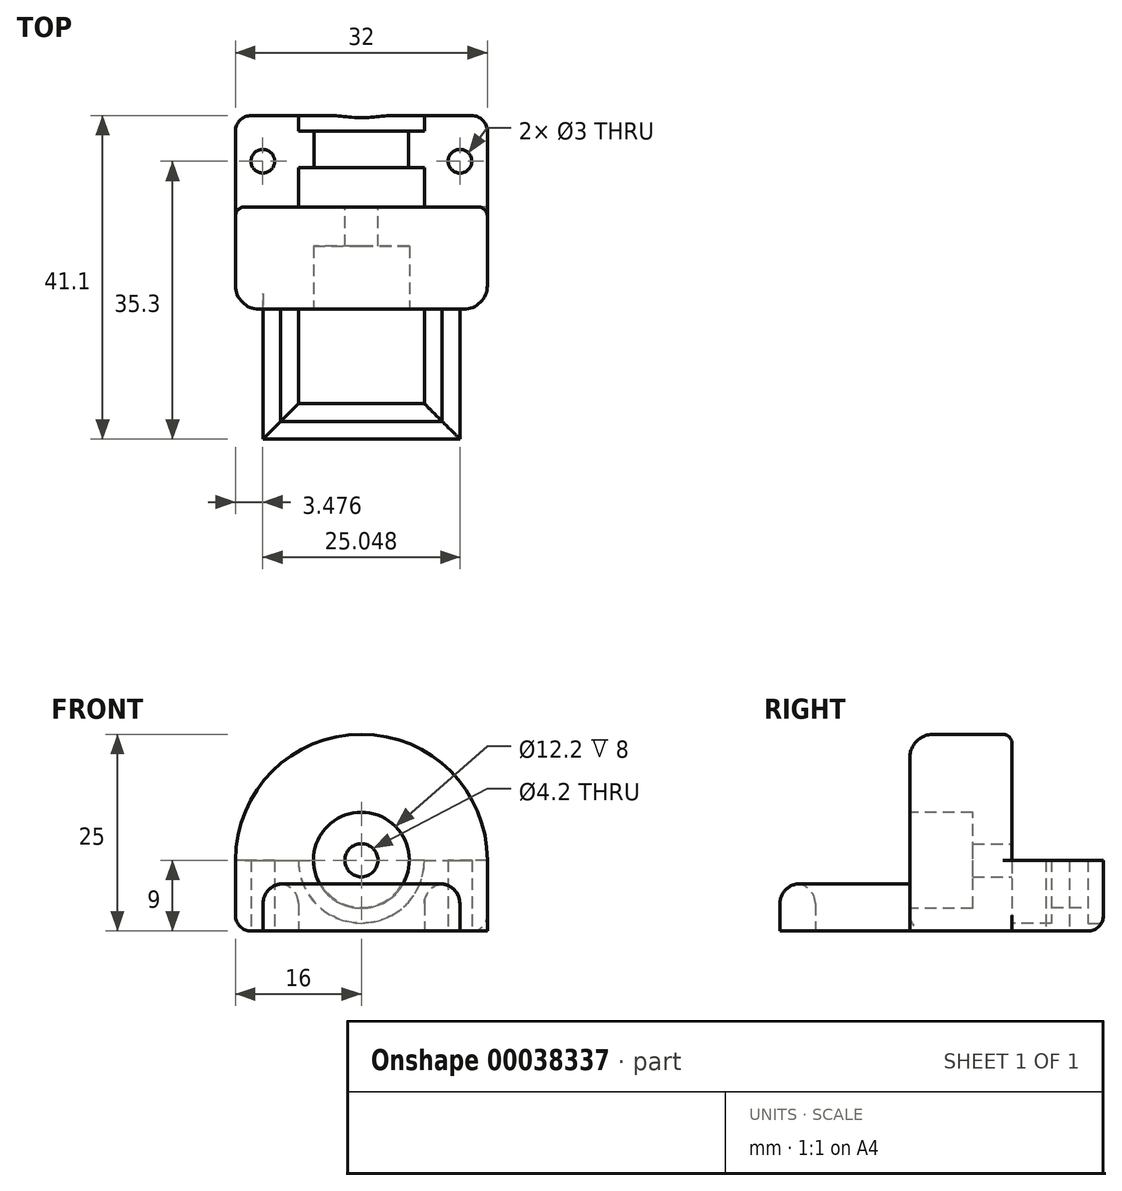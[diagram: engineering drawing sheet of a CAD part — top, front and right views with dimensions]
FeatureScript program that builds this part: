
annotation { "Feature Type Name" : "Feature", "Feature Type Description" : "" }
export const myFeature = defineFeature(function(context is Context, id is Id, definition is map)
    precondition{}
    {
        {
            var Q0;
            Q0=qCreatedBy(makeId("Top.planeOp"),FACE);
            var sketch = newSketch(context, id + "F0", { "sketchPlane" : qUnion([Q0])});
            skLineSegment(sketch, "E0.rect.bottom", {"start": v(-16, 5.8) * mm, "end": v(16, 5.8) * mm});
            skLineSegment(sketch, "E0.rect.top", {"start": v(-16, -5.8) * mm, "end": v(16, -5.8) * mm});
            skLineSegment(sketch, "E0.rect.left", {"start": v(-16, 5.8) * mm, "end": v(-16, -5.8) * mm});
            skLineSegment(sketch, "E0.rect.right", {"start": v(16, 5.8) * mm, "end": v(16, -5.8) * mm});
            skPoint(sketch, "E0.rect.middle", {"position": v(0, 0) * mm});
            skCircle(sketch, "E1", {"center": v(12.52, 0) * mm, "radius": 1.5 * mm});
            skCircle(sketch, "E2", {"center": v(-12.52, 0) * mm, "radius": 1.5 * mm});
            skSolve(sketch);
        }
        {
            var Q0;
            Q0=makeQuery(id+"F0.imprint","IMPRINT",FACE,{"disambiguationData":[TD([[makeQuery(id+"F0.imprint","IMPRINT",EDGE,{"derivedFrom":sQuery(id+"F0.wireOp",EDGE,"E0.rect.bottom")}),-1.0]])]});
            extrude(context, id + "F1", {"entities" : qUnion([Q0]), "depth" : 9 * mm});
        }
        {
            var Q0;
            Q0=makeQuery(id+"F1.opExtrude","SWEPT_FACE",FACE,{"disambiguationData":[OSD([sQuery(id+"F0.wireOp",EDGE,"E0.rect.top")])]});
            var sketch = newSketch(context, id + "F2", { "sketchPlane" : qUnion([Q0])});
            skCircle(sketch, "E3", {"center": v(0, 9) * mm, "radius": 8 * mm});
            skSolve(sketch);
        }
        {
            var Q0;
            Q0=qSketchRegion(id+"F2",true);
            var Q1;
            Q1=makeQuery(id+"F1.opExtrude","SWEPT_FACE",FACE,{"disambiguationData":[OSD([sQuery(id+"F0.wireOp",EDGE,"E0.rect.bottom")])]});
            extrude(context, id + "F3", {"entities" : qUnion([Q0, Q1]), "operationType" : NewBodyOperationType.REMOVE, "oppositeDirection" : true, "depth" : 5 * mm});
        }
        {
            var Q0;
            Q0=makeQuery(id+"F1.opExtrude","SWEPT_FACE",FACE,{"disambiguationData":[OSD([sQuery(id+"F0.wireOp",EDGE,"E0.rect.bottom")])]});
            var sketch = newSketch(context, id + "F4", { "sketchPlane" : qUnion([Q0])});
            skCircle(sketch, "E4", {"center": v(0, 9) * mm, "radius": 8 * mm});
            skSolve(sketch);
        }
        {
            var Q0;
            Q0=qSketchRegion(id+"F4",true);
            extrude(context, id + "F5", {"entities" : qUnion([Q0]), "operationType" : NewBodyOperationType.REMOVE, "oppositeDirection" : true, "depth" : 2 * mm});
        }
        {
            var Q0;
            Q0=makeQuery(id+"F5.boolean.opBoolean","COPY",FACE,{"derivedFrom":makeQuery(id+"F5.opExtrude","CAP_FACE",FACE,{"disambiguationData":[OSD([sQuery(id+"F4.wireOp",EDGE,"E4")])],"isStart":false})});
            var sketch = newSketch(context, id + "F6", { "sketchPlane" : qUnion([Q0])});
            skCircle(sketch, "E5", {"center": v(0, 9) * mm, "radius": 6 * mm});
            skSolve(sketch);
        }
        {
            var Q0;
            Q0=qSketchRegion(id+"F6",true);
            extrude(context, id + "F7", {"entities" : qUnion([Q0]), "operationType" : NewBodyOperationType.REMOVE, "oppositeDirection" : true, "depth" : 25 * mm});
        }
        {
            var Q0;
            Q0=makeQuery(id+"F1.opExtrude","CAP_EDGE",EDGE,{"disambiguationData":[OSD([sQuery(id+"F0.wireOp",EDGE,"E0.rect.bottom")])],"isStart":true});
            var Q1;
            Q1=makeQuery(id+"F7.boolean.opBoolean","COPY",EDGE,{"derivedFrom":makeQuery(id+"F7.opExtrude","CAP_EDGE",EDGE,{"disambiguationData":[OSD([sQuery(id+"F6.wireOp",EDGE,"E5")])],"isStart":true})});
            var Q2;
            Q2=makeQuery(id+"F1.opExtrude","SWEPT_EDGE",EDGE,{"disambiguationData":[OSD([sQuery(id+"F0.wireOp",EDGE,"E0.rect.bottom"),sQuery(id+"F0.wireOp",EDGE,"E0.rect.left")])]});
            var Q3;
            Q3=makeQuery(id+"F1.opExtrude","CAP_EDGE",EDGE,{"disambiguationData":[OSD([sQuery(id+"F0.wireOp",EDGE,"E0.rect.left")])],"isStart":true});
            var Q4;
            Q4=makeQuery(id+"F1.opExtrude","CAP_EDGE",EDGE,{"disambiguationData":[OSD([sQuery(id+"F0.wireOp",EDGE,"E0.rect.right")])],"isStart":true});
            var Q5;
            Q5=makeQuery(id+"F1.opExtrude","SWEPT_EDGE",EDGE,{"disambiguationData":[OSD([sQuery(id+"F0.wireOp",EDGE,"E0.rect.bottom"),sQuery(id+"F0.wireOp",EDGE,"E0.rect.right")])]});
            fillet(context, id + "F8", {"entities" : qUnion([Q0, Q1, Q2, Q3, Q4, Q5]), "radius" : 2 * mm, "tangentPropagation" : true, "allowEdgeOverflow" : false});
        }
        {
            var Q0;
            Q0=makeQuery(id+"F1.opExtrude","SWEPT_FACE",FACE,{"disambiguationData":[OSD([sQuery(id+"F0.wireOp",EDGE,"E0.rect.top")])]});
            var sketch = newSketch(context, id + "F9", { "sketchPlane" : qUnion([Q0])});
            skArc(sketch, "E6", {"start": v(16, 9) * mm, "mid": v(0, 25) * mm, "end": v(-16, 9) * mm});
            skLineSegment(sketch, "E7", {"start": v(0, 0) * mm, "end": v(13.23, 0) * mm});
            skLineSegment(sketch, "E8", {"start": v(-13.23, 0) * mm, "end": v(0, 0) * mm});
            skLineSegment(sketch, "E9", {"start": v(-16, 9) * mm, "end": v(-16, 0) * mm});
            skLineSegment(sketch, "E10", {"start": v(16, 9) * mm, "end": v(16, 0) * mm});
            skLineSegment(sketch, "E11", {"start": v(-16, 0) * mm, "end": v(16, 0) * mm});
            skSolve(sketch);
        }
        {
            var Q0;
            Q0=qSketchRegion(id+"F9",true);
            extrude(context, id + "F10", {"entities" : qUnion([Q0]), "operationType" : NewBodyOperationType.ADD, "depth" : 13 * mm});
        }
        {
            var Q0;
            Q0=qCreatedBy(makeId("Top.planeOp"),FACE);
            var sketch = newSketch(context, id + "F11", { "sketchPlane" : qUnion([Q0])});
            skLineSegment(sketch, "E12", {"start": v(-8, -18.8) * mm, "end": v(-12.5, -18.8) * mm});
            skLineSegment(sketch, "E13", {"start": v(-12.5, -18.8) * mm, "end": v(-8, -18.8) * mm});
            skLineSegment(sketch, "E14", {"start": v(12.5, -18.8) * mm, "end": v(12.5, -35.3) * mm});
            skLineSegment(sketch, "E15", {"start": v(12.5, -35.3) * mm, "end": v(-12.5, -35.3) * mm});
            skLineSegment(sketch, "E16", {"start": v(-12.5, -35.3) * mm, "end": v(-12.5, -18.8) * mm});
            skLineSegment(sketch, "E17", {"start": v(-8, -18.8) * mm, "end": v(-8, -30.8) * mm});
            skLineSegment(sketch, "E18", {"start": v(-8, -30.8) * mm, "end": v(8, -30.8) * mm});
            skLineSegment(sketch, "E19", {"start": v(8, -30.8) * mm, "end": v(8, -18.8) * mm});
            skLineSegment(sketch, "E20.trimOffspring", {"start": v(8, -18.8) * mm, "end": v(12.5, -18.8) * mm});
            skPoint(sketch, "E21.orphan", {"position": v(0, -18.8) * mm});
            skPoint(sketch, "E22", {"position": v(0, -30.8) * mm});
            skPoint(sketch, "E23", {"position": v(0, -35.3) * mm});
            skSolve(sketch);
        }
        {
            var Q0;
            Q0=qSketchRegion(id+"F11",true);
            extrude(context, id + "F12", {"entities" : qUnion([Q0]), "operationType" : NewBodyOperationType.ADD, "depth" : 6 * mm});
        }
        {
            var Q0;
            Q0=makeQuery(id+"F12.opExtrude","CAP_EDGE",EDGE,{"disambiguationData":[OSD([sQuery(id+"F11.wireOp",EDGE,"E17")])],"isStart":false});
            var Q1;
            Q1=makeQuery(id+"F12.opExtrude","CAP_EDGE",EDGE,{"disambiguationData":[OSD([sQuery(id+"F11.wireOp",EDGE,"E16")])],"isStart":false});
            var Q2;
            Q2=makeQuery(id+"F12.opExtrude","CAP_EDGE",EDGE,{"disambiguationData":[OSD([sQuery(id+"F11.wireOp",EDGE,"E19")])],"isStart":false});
            var Q3;
            Q3=makeQuery(id+"F12.opExtrude","CAP_EDGE",EDGE,{"disambiguationData":[OSD([sQuery(id+"F11.wireOp",EDGE,"E14")])],"isStart":false});
            var Q4;
            Q4=makeQuery(id+"F12.opExtrude","CAP_EDGE",EDGE,{"disambiguationData":[OSD([sQuery(id+"F11.wireOp",EDGE,"E18")])],"isStart":false});
            var Q5;
            Q5=makeQuery(id+"F12.opExtrude","CAP_EDGE",EDGE,{"disambiguationData":[OSD([sQuery(id+"F11.wireOp",EDGE,"E15")])],"isStart":false});
            fillet(context, id + "F13", {"entities" : qUnion([Q0, Q1, Q2, Q3, Q4, Q5]), "radius" : 2.5 * mm, "tangentPropagation" : true, "allowEdgeOverflow" : false});
        }
        {
            var Q0;
            Q0=makeQuery(id+"F10.opExtrude","CAP_EDGE",EDGE,{"disambiguationData":[OSD([sQuery(id+"F9.wireOp",EDGE,"E6")])],"isStart":false});
            fillet(context, id + "F14", {"entities" : qUnion([Q0]), "radius" : 3 * mm, "tangentPropagation" : true, "allowEdgeOverflow" : false});
        }
        {
            var Q0;
            Q0=makeQuery(id+"F10.opExtrude","CAP_EDGE",EDGE,{"disambiguationData":[OSD([sQuery(id+"F9.wireOp",EDGE,"E6")])],"isStart":true});
            fillet(context, id + "F15", {"entities" : qUnion([Q0]), "radius" : 1.2 * mm, "tangentPropagation" : true, "allowEdgeOverflow" : false});
        }
        {
            var Q0;
            Q0=makeQuery(id+"F10.opExtrude","CAP_FACE",FACE,{"disambiguationData":[OSD([sQuery(id+"F9.wireOp",EDGE,"E6"),sQuery(id+"F9.wireOp",EDGE,"E9"),sQuery(id+"F9.wireOp",EDGE,"E10"),sQuery(id+"F9.wireOp",EDGE,"E11")])],"isStart":false});
            var sketch = newSketch(context, id + "F16", { "sketchPlane" : qUnion([Q0])});
            skCircle(sketch, "E24", {"center": v(0, 9) * mm, "radius": 6.1 * mm});
            skSolve(sketch);
        }
        {
            var Q0;
            Q0=qSketchRegion(id+"F16",true);
            extrude(context, id + "F17", {"entities" : qUnion([Q0]), "operationType" : NewBodyOperationType.REMOVE, "oppositeDirection" : true, "depth" : 8 * mm});
        }
        {
            var Q0;
            Q0=makeQuery(id+"F14.opFillet","BLEND_EDGE",EDGE,{"blendedFrom":[makeQuery(id+"F10.opExtrude","CAP_EDGE",EDGE,{"disambiguationData":[OSD([sQuery(id+"F9.wireOp",EDGE,"E9")])],"isStart":false}),makeQuery(id+"F10.boolean.opBoolean","MERGE",FACE,{"derivedFrom":[makeQuery(id+"F1.opExtrude","CAP_FACE",FACE,{"disambiguationData":[OSD([sQuery(id+"F0.wireOp",EDGE,"E0.rect.bottom"),sQuery(id+"F0.wireOp",EDGE,"E0.rect.top"),sQuery(id+"F0.wireOp",EDGE,"E0.rect.left"),sQuery(id+"F0.wireOp",EDGE,"E0.rect.right"),sQuery(id+"F0.wireOp",EDGE,"E1"),sQuery(id+"F0.wireOp",EDGE,"E2")])],"isStart":true}),makeQuery(id+"F10.opExtrude","SWEPT_FACE",FACE,{"disambiguationData":[OSD([sQuery(id+"F9.wireOp",EDGE,"E11")])]})]})],"blendedInto":[makeQuery(id+"F10.boolean.opBoolean","MERGE",FACE,{"derivedFrom":[makeQuery(id+"F1.opExtrude","CAP_FACE",FACE,{"disambiguationData":[OSD([sQuery(id+"F0.wireOp",EDGE,"E0.rect.bottom"),sQuery(id+"F0.wireOp",EDGE,"E0.rect.top"),sQuery(id+"F0.wireOp",EDGE,"E0.rect.left"),sQuery(id+"F0.wireOp",EDGE,"E0.rect.right"),sQuery(id+"F0.wireOp",EDGE,"E1"),sQuery(id+"F0.wireOp",EDGE,"E2")])],"isStart":true}),makeQuery(id+"F10.opExtrude","SWEPT_FACE",FACE,{"disambiguationData":[OSD([sQuery(id+"F9.wireOp",EDGE,"E11")])]})]})]});
            fillet(context, id + "F18", {"entities" : qUnion([Q0]), "radius" : 2 * mm, "tangentPropagation" : true, "allowEdgeOverflow" : false});
        }
        {
            var Q0;
            {var subQ0=sQuery(id+"F9.wireOp",EDGE,"E6");var subQ1=sQuery(id+"F9.wireOp",EDGE,"E9");var subQ2=sQuery(id+"F9.wireOp",EDGE,"E10");Q0=makeQuery(id+"F10.boolean.opBoolean","SPLIT",FACE,{"disambiguationData":[TD([makeQuery(id+"F3.boolean.opBoolean","COPY",FACE,{"derivedFrom":makeQuery(id+"F3.opExtrude","SWEPT_FACE",FACE,{"disambiguationData":[OSD([sQuery(id+"F2.wireOp",EDGE,"E3")])]})})])],"derivedFrom":makeQuery(id+"F10.opExtrude","CAP_FACE",FACE,{"disambiguationData":[OSD([subQ0,subQ1,subQ2,sQuery(id+"F9.wireOp",EDGE,"E11")])],"isStart":true})});}
            var sketch = newSketch(context, id + "F19", { "sketchPlane" : qUnion([Q0])});
            skCircle(sketch, "E25", {"center": v(0, 9) * mm, "radius": 2.1 * mm});
            skSolve(sketch);
        }
        {
            var Q0;
            Q0=qSketchRegion(id+"F19",true);
            extrude(context, id + "F20", {"entities" : qUnion([Q0]), "operationType" : NewBodyOperationType.REMOVE, "oppositeDirection" : true, "depth" : 7 * mm});
        }
    });
